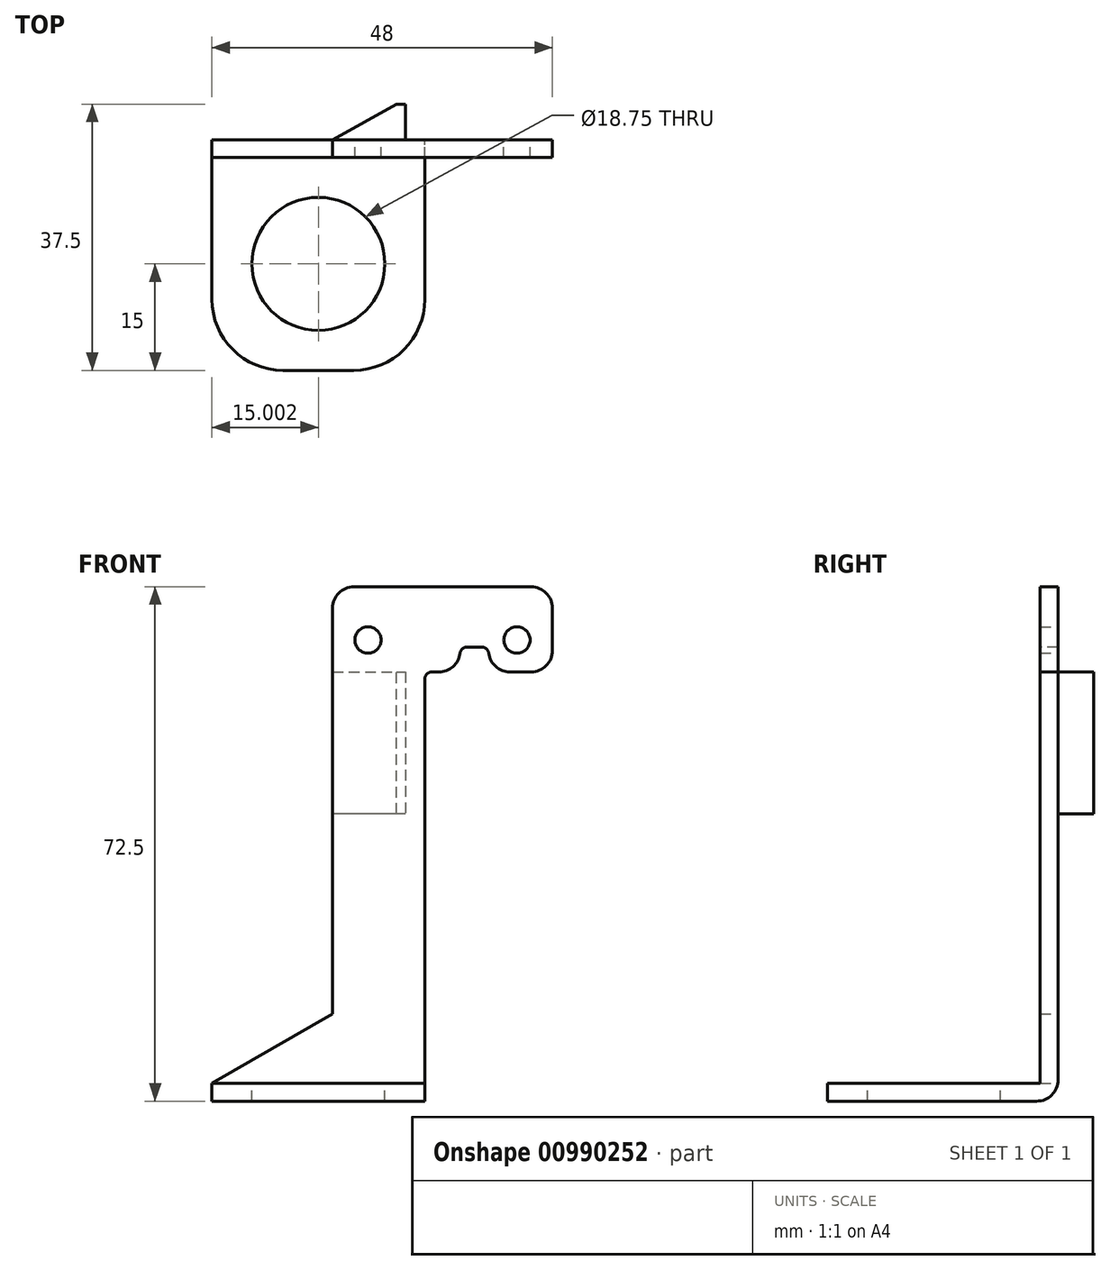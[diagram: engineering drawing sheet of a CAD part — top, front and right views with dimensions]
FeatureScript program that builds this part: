
annotation { "Feature Type Name" : "Feature", "Feature Type Description" : "" }
export const myFeature = defineFeature(function(context is Context, id is Id, definition is map)
    precondition{}
    {
        {
            var Q0;
            Q0=qCreatedBy(makeId("Front.planeOp"),FACE);
            var sketch = newSketch(context, id + "F0", { "sketchPlane" : qUnion([Q0])});
            skLineSegment(sketch, "E0.bottom", {"start": v(-17.95, 19.99) * mm, "end": v(13.05, 19.99) * mm});
            skLineSegment(sketch, "E0.top", {"start": v(-17.95, 7.99) * mm, "end": v(2.65, 7.99) * mm});
            skLineSegment(sketch, "E0.left", {"start": v(-17.95, 19.99) * mm, "end": v(-17.95, 7.99) * mm});
            skLineSegment(sketch, "E0.right", {"start": v(13.05, 19.99) * mm, "end": v(13.05, 7.99) * mm});
            skLineSegment(sketch, "E1.bottom", {"start": v(-4.95, 7.99) * mm, "end": v(-17.95, 7.99) * mm});
            skLineSegment(sketch, "E1.top", {"start": v(-4.95, -52.51) * mm, "end": v(-34.95, -52.51) * mm});
            skLineSegment(sketch, "E1.left", {"start": v(-4.95, 7.99) * mm, "end": v(-4.95, -52.51) * mm});
            skLineSegment(sketch, "E1.right", {"start": v(-17.95, 7.99) * mm, "end": v(-17.95, -50.01) * mm});
            skLineSegment(sketch, "E2.bottom", {"start": v(-34.95, -52.51) * mm, "end": v(-4.95, -52.51) * mm});
            skLineSegment(sketch, "E2.top", {"start": v(-17.95, -50.01) * mm, "end": v(-4.95, -50.01) * mm});
            skLineSegment(sketch, "E2.right", {"start": v(-4.95, -52.51) * mm, "end": v(-4.95, -50.01) * mm});
            skPoint(sketch, "E3", {"position": v(-12.95, 12.49) * mm});
            skPoint(sketch, "E4", {"position": v(8.05, 12.49) * mm});
            skLineSegment(sketch, "E5", {"start": v(-17.95, -50.01) * mm, "end": v(-34.95, -50.01) * mm});
            skLineSegment(sketch, "E6", {"start": v(-34.95, -50.01) * mm, "end": v(-34.95, -52.51) * mm});
            skPoint(sketch, "E7", {"position": v(-19.95, -52.51) * mm});
            skLineSegment(sketch, "E8.top", {"start": v(0.05, 11.49) * mm, "end": v(4.05, 11.49) * mm});
            skLineSegment(sketch, "E8.left", {"start": v(4.05, 7.99) * mm, "end": v(4.05, 11.49) * mm});
            skLineSegment(sketch, "E8.right", {"start": v(0.05, 7.99) * mm, "end": v(0.05, 11.49) * mm});
            skLineSegment(sketch, "E9.trimOffspring", {"start": v(4.05, 7.99) * mm, "end": v(13.05, 7.99) * mm});
            skLineSegment(sketch, "E10.top", {"start": v(-4.95, -12.01) * mm, "end": v(-17.95, -12.01) * mm});
            skLineSegment(sketch, "E10.left", {"start": v(-4.95, 7.99) * mm, "end": v(-4.95, -12.01) * mm});
            skLineSegment(sketch, "E10.right", {"start": v(-17.95, 7.99) * mm, "end": v(-17.95, -12.01) * mm});
            skLineSegment(sketch, "E11", {"start": v(-34.95, -50.01) * mm, "end": v(-17.95, -40.2) * mm});
            skLineSegment(sketch, "E12", {"start": v(-7.65, 7.99) * mm, "end": v(-7.65, -12.01) * mm});
            skLineSegment(sketch, "E13", {"start": v(-4.95, 7.99) * mm, "end": v(0.05, 7.99) * mm});
            skSolve(sketch);
        }
        {
            var Q0;
            Q0=makeQuery(id+"F0.imprint","IMPRINT",FACE,{"disambiguationData":[TD([[makeQuery(id+"F0.imprint","IMPRINT",EDGE,{"derivedFrom":sQuery(id+"F0.wireOp",EDGE,"E0.bottom")}),-1.0]])]});
            var Q1;
            Q1=makeQuery(id+"F0.imprint","IMPRINT",FACE,{"disambiguationData":[TD([[makeQuery(id+"F0.imprint","IMPRINT",EDGE,{"derivedFrom":sQuery(id+"F0.wireOp",EDGE,"E1.bottom")}),1.0]])]});
            var Q2;
            {var subQ0=sQuery(id+"F0.wireOp",EDGE,"E5");Q2=makeQuery(id+"F0.imprint","IMPRINT",FACE,{"disambiguationData":[TD([[makeQuery(id+"F0.imprint","IMPRINT",EDGE,{"derivedFrom":subQ0}),-1.0]])]});}
            var Q3;
            {var subQ0=sQuery(id+"F0.wireOp",EDGE,"E12");var subQ7=makeQuery(id+"F0.imprint","IMPRINT",EDGE,{"derivedFrom":subQ0});Q3=qUnion([makeQuery(id+"F0.imprint","IMPRINT",FACE,{"disambiguationData":[TD([[subQ7,-1.0]])]}),makeQuery(id+"F0.imprint","IMPRINT",FACE,{"disambiguationData":[TD([[subQ7,1.0]])]})]);}
            var Q4;
            {var subQ0=sQuery(id+"F0.wireOp",EDGE,"E2.top");Q4=makeQuery(id+"F0.imprint","IMPRINT",FACE,{"disambiguationData":[TD([[makeQuery(id+"F0.imprint","IMPRINT",EDGE,{"derivedFrom":subQ0}),1.0]])]});}
            var Q5;
            {var subQ3=sQuery(id+"F0.wireOp",EDGE,"E12");Q5=makeQuery(id+"F0.imprint","IMPRINT",FACE,{"disambiguationData":[TD([[makeQuery(id+"F0.imprint","IMPRINT",EDGE,{"derivedFrom":subQ3}),-1.0]])]});}
            extrude(context, id + "F1", {"entities" : qUnion([Q0, Q1, Q2, Q3, Q4, Q5]), "depth" : 2.5 * mm, "offsetDistance" : 25 * mm});
        }
        {
            var Q0;
            {var subQ2=sQuery(id+"F0.wireOp",EDGE,"E1.top");Q0=makeQuery(id+"F0.imprint","IMPRINT",FACE,{"disambiguationData":[TD([[makeQuery(id+"F0.imprint","IMPRINT",EDGE,{"derivedFrom":subQ2}),-1.0]])]});}
            extrude(context, id + "F2", {"entities" : qUnion([Q0]), "operationType" : NewBodyOperationType.ADD, "depth" : 32.5 * mm, "offsetDistance" : 25 * mm});
        }
        {
            var Q0;
            Q0=qCreatedBy(makeId("Top.planeOp"),FACE);
            var sketch = newSketch(context, id + "F3", { "sketchPlane" : qUnion([Q0])});
            skLineSegment(sketch, "E14.0.1", {"start": v(-34.95, -2.5) * mm, "end": v(-34.95, -32.5) * mm});
            skLineSegment(sketch, "E14.0.3", {"start": v(-4.95, -32.5) * mm, "end": v(-4.95, -2.5) * mm});
            skPoint(sketch, "E15.0", {"position": v(-19.95, -32.5) * mm});
            skPoint(sketch, "E16.0", {"position": v(-4.95, -17.5) * mm});
            skPoint(sketch, "E17", {"position": v(-19.95, -17.5) * mm});
            skSolve(sketch);
        }
        {
            var Q0;
            Q0=sQuery(id+"F3.wireOp",VERTEX,"E17");
            var Q1;
            Q1=makeQuery(id+"F1.opExtrude","SWEPT_BODY",BODY,{"disambiguationData":[OSD([sQuery(id+"F0.wireOp",EDGE,"E0.bottom"),sQuery(id+"F0.wireOp",EDGE,"E0.top"),sQuery(id+"F0.wireOp",EDGE,"E0.left"),sQuery(id+"F0.wireOp",EDGE,"E0.right"),sQuery(id+"F0.wireOp",EDGE,"E1.left"),sQuery(id+"F0.wireOp",EDGE,"E1.right"),sQuery(id+"F0.wireOp",EDGE,"E2.top"),sQuery(id+"F0.wireOp",EDGE,"E5"),sQuery(id+"F0.wireOp",EDGE,"E8.top"),sQuery(id+"F0.wireOp",EDGE,"E8.left"),sQuery(id+"F0.wireOp",EDGE,"E8.right"),sQuery(id+"F0.wireOp",EDGE,"E9.trimOffspring"),sQuery(id+"F0.wireOp",EDGE,"E11")])]});
            hole(context, id + "F4", {"style" : HoleStyle.SIMPLE, "endStyle" : HoleEndStyle.THROUGH, "holeDiameter" : 18.75 * mm, "majorDiameter" : 6 * mm, "isTappedThrough" : true, "tappedDepth" : 12 * mm, "tapClearance" : 3, "locations" : qUnion([Q0]), "scope" : qUnion([Q1])});
        }
        {
            var Q0;
            Q0=sQuery(id+"F0.wireOp",VERTEX,"E3");
            var Q1;
            Q1=sQuery(id+"F0.wireOp",VERTEX,"E4");
            var Q2;
            Q2=makeQuery(id+"F1.opExtrude","SWEPT_BODY",BODY,{"disambiguationData":[OSD([sQuery(id+"F0.wireOp",EDGE,"E0.bottom"),sQuery(id+"F0.wireOp",EDGE,"E0.top"),sQuery(id+"F0.wireOp",EDGE,"E0.left"),sQuery(id+"F0.wireOp",EDGE,"E0.right"),sQuery(id+"F0.wireOp",EDGE,"E1.left"),sQuery(id+"F0.wireOp",EDGE,"E1.right"),sQuery(id+"F0.wireOp",EDGE,"E2.top"),sQuery(id+"F0.wireOp",EDGE,"E5"),sQuery(id+"F0.wireOp",EDGE,"E8.top"),sQuery(id+"F0.wireOp",EDGE,"E8.left"),sQuery(id+"F0.wireOp",EDGE,"E8.right"),sQuery(id+"F0.wireOp",EDGE,"E9.trimOffspring"),sQuery(id+"F0.wireOp",EDGE,"E11")])]});
            hole(context, id + "F5", {"style" : HoleStyle.SIMPLE, "endStyle" : HoleEndStyle.THROUGH, "oppositeDirection" : true, "holeDiameter" : 3.7 * mm, "majorDiameter" : 5 * mm, "isTappedThrough" : true, "tappedDepth" : 12 * mm, "tapClearance" : 3, "locations" : qUnion([Q0, Q1]), "scope" : qUnion([Q2])});
        }
        {
            var Q0;
            {var subQ3=sQuery(id+"F0.wireOp",EDGE,"E12");Q0=makeQuery(id+"F0.imprint","IMPRINT",FACE,{"disambiguationData":[TD([[makeQuery(id+"F0.imprint","IMPRINT",EDGE,{"derivedFrom":subQ3}),-1.0]])]});}
            extrude(context, id + "F6", {"entities" : qUnion([Q0]), "operationType" : NewBodyOperationType.ADD, "oppositeDirection" : true, "depth" : 5 * mm, "offsetDistance" : 25 * mm});
        }
        {
            var Q0;
            Q0=makeQuery(id+"F6.opExtrude","CAP_EDGE",EDGE,{"disambiguationData":[OSD([sQuery(id+"F0.wireOp",EDGE,"E1.right")])],"isStart":false});
            chamfer(context, id + "F7", {"entities" : qUnion([Q0]), "chamferType" : ChamferType.TWO_OFFSETS, "width1" : 5 * mm, "oppositeDirection" : false, "width2" : 9 * mm, "tangentPropagation" : true});
        }
        {
            var Q0;
            Q0=makeQuery(id+"F2.opExtrude","CAP_EDGE",EDGE,{"disambiguationData":[OSD([sQuery(id+"F0.wireOp",EDGE,"E1.left")])],"isStart":false});
            var Q1;
            Q1=makeQuery(id+"F2.opExtrude","CAP_EDGE",EDGE,{"disambiguationData":[OSD([sQuery(id+"F0.wireOp",EDGE,"E6")])],"isStart":false});
            fillet(context, id + "F8", {"entities" : qUnion([Q0, Q1]), "radius" : 10 * mm, "tangentPropagation" : true, "allowEdgeOverflow" : false});
        }
        {
            var Q0;
            Q0=makeQuery(id+"F1.opExtrude","SWEPT_EDGE",EDGE,{"disambiguationData":[OSD([sQuery(id+"F0.wireOp",EDGE,"E0.bottom"),sQuery(id+"F0.wireOp",EDGE,"E0.left")])]});
            var Q1;
            Q1=makeQuery(id+"F1.opExtrude","SWEPT_EDGE",EDGE,{"disambiguationData":[OSD([sQuery(id+"F0.wireOp",EDGE,"E0.bottom"),sQuery(id+"F0.wireOp",EDGE,"E0.right")])]});
            var Q2;
            Q2=makeQuery(id+"F1.opExtrude","SWEPT_EDGE",EDGE,{"disambiguationData":[OSD([sQuery(id+"F0.wireOp",EDGE,"E0.top"),sQuery(id+"F0.wireOp",EDGE,"E8.right")])]});
            var Q3;
            Q3=makeQuery(id+"F1.opExtrude","SWEPT_EDGE",EDGE,{"disambiguationData":[OSD([sQuery(id+"F0.wireOp",EDGE,"E8.left"),sQuery(id+"F0.wireOp",EDGE,"E9.trimOffspring")])]});
            var Q4;
            Q4=makeQuery(id+"F1.opExtrude","SWEPT_EDGE",EDGE,{"disambiguationData":[OSD([sQuery(id+"F0.wireOp",EDGE,"E0.right"),sQuery(id+"F0.wireOp",EDGE,"E9.trimOffspring")])]});
            var Q5;
            Q5=makeQuery(id+"F2.opExtrude","CAP_EDGE",EDGE,{"disambiguationData":[OSD([sQuery(id+"F0.wireOp",EDGE,"E1.top")])],"isStart":true});
            var Q6;
            Q6=makeQuery(id+"F1.opExtrude","CAP_EDGE",EDGE,{"disambiguationData":[OSD([sQuery(id+"F0.wireOp",EDGE,"E2.top"),sQuery(id+"F0.wireOp",EDGE,"E5")])],"isStart":false});
            fillet(context, id + "F9", {"entities" : qUnion([Q0, Q1, Q2, Q3, Q4, Q5, Q6]), "radius" : 3 * mm, "allowEdgeOverflow" : false});
        }
        {
            var Q0;
            Q0=makeQuery(id+"F1.opExtrude","SWEPT_EDGE",EDGE,{"disambiguationData":[OSD([sQuery(id+"F0.wireOp",EDGE,"E8.top"),sQuery(id+"F0.wireOp",EDGE,"E8.right")])]});
            var Q1;
            Q1=makeQuery(id+"F1.opExtrude","SWEPT_EDGE",EDGE,{"disambiguationData":[OSD([sQuery(id+"F0.wireOp",EDGE,"E8.top"),sQuery(id+"F0.wireOp",EDGE,"E8.left")])]});
            var Q2;
            Q2=makeQuery(id+"F1.opExtrude","SWEPT_EDGE",EDGE,{"disambiguationData":[OSD([sQuery(id+"F0.wireOp",EDGE,"E0.top"),sQuery(id+"F0.wireOp",EDGE,"E1.left")])]});
            fillet(context, id + "F10", {"entities" : qUnion([Q0, Q1, Q2]), "radius" : 1 * mm, "tangentPropagation" : true, "allowEdgeOverflow" : false});
        }
    });
